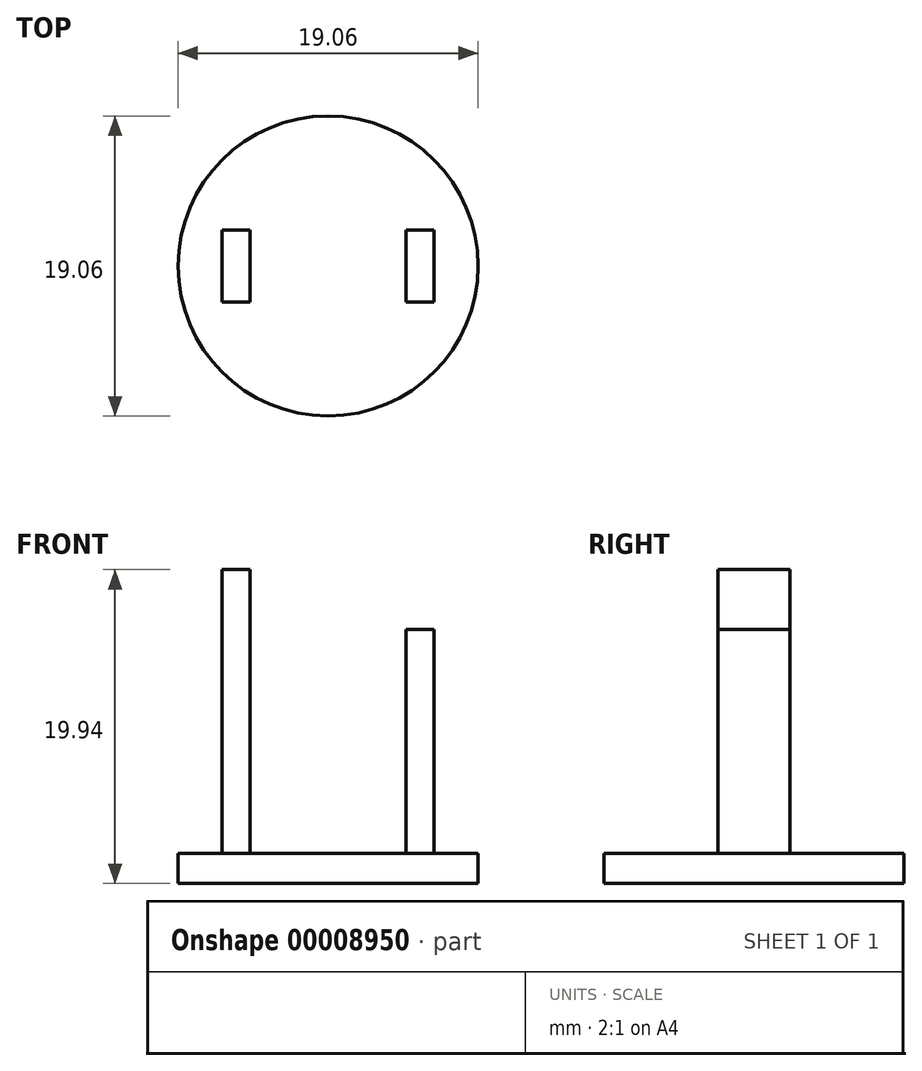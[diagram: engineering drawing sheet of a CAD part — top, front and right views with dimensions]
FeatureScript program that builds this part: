
annotation { "Feature Type Name" : "Feature", "Feature Type Description" : "" }
export const myFeature = defineFeature(function(context is Context, id is Id, definition is map)
    precondition{}
    {
        {
            var Q0;
            Q0=qCreatedBy(makeId("Top.planeOp"),FACE);
            var sketch = newSketch(context, id + "F0", { "sketchPlane" : qUnion([Q0])});
            skCircle(sketch, "E0", {"center": v(0, 0) * mm, "radius": 9.53 * mm});
            skSolve(sketch);
        }
        {
            var Q0;
            Q0=makeQuery(id+"F0.imprint","IMPRINT",FACE,{"disambiguationData":[TD([[makeQuery(id+"F0.imprint","IMPRINT",EDGE,{"derivedFrom":sQuery(id+"F0.wireOp",EDGE,"E0")}),1.0]])]});
            extrude(context, id + "F1", {"entities" : qUnion([Q0]), "depth" : 1.9 * mm});
        }
        {
            var Q0;
            Q0=makeQuery(id+"F1.opExtrude","CAP_FACE",FACE,{"disambiguationData":[OSD([sQuery(id+"F0.wireOp",EDGE,"E0")])],"isStart":false});
            var sketch = newSketch(context, id + "F2", { "sketchPlane" : qUnion([Q0])});
            skLineSegment(sketch, "E1.bottom", {"start": v(-6.73, 2.29) * mm, "end": v(-4.95, 2.29) * mm});
            skLineSegment(sketch, "E1.top", {"start": v(-6.73, -2.29) * mm, "end": v(-4.95, -2.29) * mm});
            skLineSegment(sketch, "E1.left", {"start": v(-6.73, 2.29) * mm, "end": v(-6.73, -2.29) * mm});
            skLineSegment(sketch, "E1.right", {"start": v(-4.95, 2.29) * mm, "end": v(-4.95, -2.29) * mm});
            skLineSegment(sketch, "E2", {"start": v(0, 9.53) * mm, "end": v(0, -9.53) * mm, "construction": true});
            skLineSegment(sketch, "E3.0.MirrorCS", {"start": v(4.95, 2.29) * mm, "end": v(4.95, -2.29) * mm});
            skLineSegment(sketch, "E4.0.MirrorCS", {"start": v(6.73, 2.29) * mm, "end": v(4.95, 2.29) * mm});
            skLineSegment(sketch, "E5.0.MirrorCS", {"start": v(6.73, 2.29) * mm, "end": v(6.73, -2.29) * mm});
            skLineSegment(sketch, "E6.0.MirrorCS", {"start": v(6.73, -2.29) * mm, "end": v(4.95, -2.29) * mm});
            skSolve(sketch);
        }
        {
            var Q0;
            Q0=makeQuery(id+"F2.imprint","IMPRINT",FACE,{"disambiguationData":[TD([[makeQuery(id+"F2.imprint","IMPRINT",EDGE,{"derivedFrom":sQuery(id+"F2.wireOp",EDGE,"E1.bottom")}),-1.0]])]});
            extrude(context, id + "F3", {"entities" : qUnion([Q0]), "operationType" : NewBodyOperationType.ADD, "depth" : 18.03 * mm});
        }
        {
            var Q0;
            Q0=makeQuery(id+"F2.imprint","IMPRINT",FACE,{"disambiguationData":[TD([[makeQuery(id+"F2.imprint","IMPRINT",EDGE,{"derivedFrom":sQuery(id+"F2.wireOp",EDGE,"E3.0.MirrorCS")}),1.0]])]});
            extrude(context, id + "F4", {"entities" : qUnion([Q0]), "operationType" : NewBodyOperationType.ADD, "depth" : 14.22 * mm});
        }
    });
